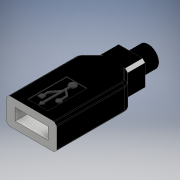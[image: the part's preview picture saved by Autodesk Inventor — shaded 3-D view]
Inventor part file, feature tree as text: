
AUTODESK INVENTOR PART (.ipt)
format: ipt  version: 2018 (Build 220112000, 112)  size: 336,384 bytes
history: native  units: mm
features: sketch x8, extrude x6, fillet x3, chamfer x2, plane x1
ambient origin geometry x8: Origin, YZ Plane, XZ Plane, XY Plane, X Axis, Y Axis, Z Axis, Center Point
bodies: Solid1 (feature_tree)
feature tree (20):
  extrude  "Extrusion1"  Depth=26.93mm
  chamfer  "Chamfer1"  Distance=10.0mm
  fillet  "Fillet1"  Radius=0.5mm
  fillet  "Fillet2"  Radius=3.0mm
  fillet  "Fillet3"  Radius=3.0mm
  extrude  "Extrusion2"  Depth=14.9mm
  extrude  "Extrusion7"  Depth=0.3mm TaperAngle=0.0deg
  plane  "Work Plane1"
  extrude  "Extrusion14"  Depth=12.5mm
  sketch  "Sketch18"  dims[d14=7.75mm d15=14.9mm]
  sketch  "Sketch19"  dims[d16=2.3mm d17=0.3mm d18=0.0mm]
  extrude  "Extrusion15"  Depth=6.75mm TaperAngle=0.0deg
  chamfer  "Chamfer2"  Distance=2.26mm
  extrude  "Extrusion16"  Depth=11.04mm
  sketch  "Sketch1"  dims[d2=19.05mm d3=26.93mm]
  sketch  "Sketch2"  dims[d4=11.04mm]
  sketch  "Sketch8"  dims[d5=4.0mm d6=10.0mm d7=0.0mm]
  sketch  "Sketch17"  dims[d8=1.0mm d9=2.0mm d10=45.0deg d11=0.5mm d12=3.0mm d13=3.0mm]
  sketch  "Sketch20"  dims[d71=0.3mm d72=0.0mm d101=12.5mm]
  sketch  "Sketch21"  dims[d102=4.52mm d106=20.0mm d107=0.0mm d108=2.26mm d109=11.04mm d110=6.6mm d111=0.0mm d112=1.0mm d113=2.0mm d114=45.0deg d115=7.9mm d116=6.75mm d117=0.0mm]
